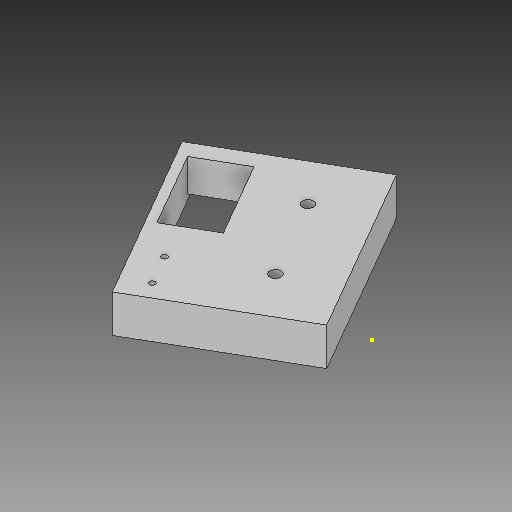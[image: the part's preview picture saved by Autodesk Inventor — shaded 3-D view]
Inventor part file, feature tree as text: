
AUTODESK INVENTOR PART (.ipt)
format: ipt  version: 2017 (Build 210142000, 142)  size: 223,744 bytes
history: native  units: in
note: dims shown in document units (in); Inventor stores cm internally (conversion verified against a paired STEP export)
features: sketch x7, extrude x6, projected_geometry x5, imported_body x1
ambient origin geometry x8: Origin, YZ Plane, XZ Plane, XY Plane, X Axis, Y Axis, Z Axis, Center Point
bodies: Solid1 (feature_tree)
feature tree (19):
  extrude  "Extrusion1"  Depth=0.3937in TaperAngle=0.0deg
  extrude  "Extrusion2"  Depth=0.3937in TaperAngle=0.0deg
  extrude  "Extrusion4"  Depth=0.3937in TaperAngle=0.0deg
  extrude  "Extrusion5"  Depth=0.3937in TaperAngle=0.0deg
  extrude  "Extrusion6"  Depth=0.188in
  extrude  "limit switch"  Depth=0.125in
  sketch  "Sketch9"  dims[d19=0.3937in d20=0.0in d21=0.276in d22=0.2in d23=0.575in d24=0.063in d25=0.3937in d26=0.0in]
  sketch  "Sketch1"  dims[d0=1.25in d1=0.3937in d2=0.0in]
  projected_geometry  "Projected Loop1"
  sketch  "Sketch2"  dims[d3=0.125in d4=0.3937in d5=0.0in]
  sketch  "Sketch4"  dims[d9=0.4331in d10=0.3937in d11=0.0in]
  projected_geometry  "Projected Loop3"
  sketch  "Sketch5"  dims[d12=0.3937in d13=0.3937in d14=0.0in]
  projected_geometry  "Projected Loop4"
  sketch  "Sketch6"  dims[d15=0.765in d16=0.188in]
  projected_geometry  "Projected Loop5"
  sketch  "Sketch7"  dims[d17=0.5in d18=0.125in]
  projected_geometry  "Projected Loop6"
  imported_body  "Base1"
